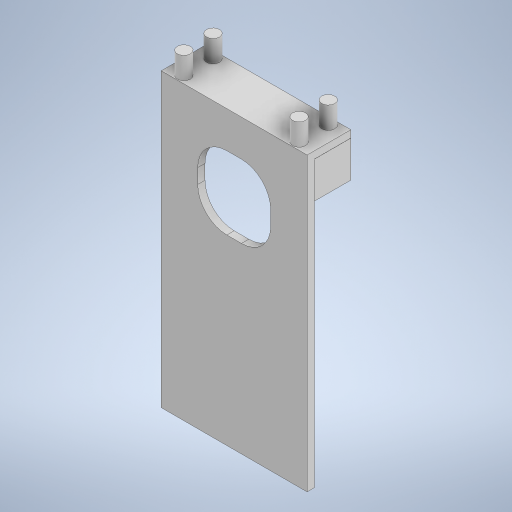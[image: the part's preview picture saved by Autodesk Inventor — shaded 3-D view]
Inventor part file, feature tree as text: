
AUTODESK INVENTOR PART (.ipt)
format: ipt  version: 2023 (Build 270158000, 158)  size: 309,760 bytes
history: native  units: mm
features: extrude x7, sketch x7
ambient origin geometry x8: Origin, YZ Plane, XZ Plane, XY Plane, X Axis, Y Axis, Z Axis, Center Point
bodies: Solid1 (feature_tree)
feature tree (14):
  extrude  "Extrusion1"  Depth=200.0mm
  extrude  "Extrusion6"  Depth=50.0mm
  sketch  "Sketch15"  dims[d22=50.0mm d23=20.0mm]
  sketch  "Sketch16"  dims[d24=5.0mm d25=0.0mm d46=100.0mm]
  extrude  "Extrusion11"  Depth=20.0mm
  extrude  "Extrusion12"  Depth=100.0mm
  extrude  "Extrusion13"  Depth=30.0mm
  extrude  "Extrusion14"  Depth=9.0mm
  extrude  "Extrusion16"  Depth=5.0mm TaperAngle=0.0deg
  sketch  "Sketch1"  dims[d0=100.0mm d1=200.0mm]
  sketch  "Sketch6"  dims[d2=5.0mm d3=0.0mm d21=50.0mm]
  sketch  "Sketch17"  dims[d47=30.0mm d48=9.0mm]
  sketch  "Sketch18"  dims[d49=9.0mm d50=9.0mm]
  sketch  "Sketch20"  dims[d51=9.0mm d52=5.0mm d53=0.0mm d54=15.0mm d55=0.0mm d56=100.0mm d57=30.0mm d58=5.0mm d59=0.0mm d60=5.0mm d61=0.0mm d64=5.0mm d65=0.0mm]
